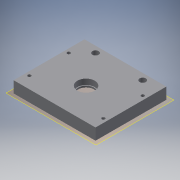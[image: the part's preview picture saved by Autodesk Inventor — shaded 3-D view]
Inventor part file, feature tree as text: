
AUTODESK INVENTOR PART (.ipt)
format: ipt  version: 2017 (Build 210142000, 142)  size: 169,472 bytes
history: native  units: mm
features: extrude x4, sketch x4, reference x2, projected_geometry x2, other x2, plane x1
ambient origin geometry x8: Origin, YZ Plane, XZ Plane, XY Plane, X Axis, Y Axis, Z Axis, Center Point
bodies: Solid1 (feature_tree)
feature tree (15):
  plane  "Work Plane1"
  extrude  "Extrusion1"  Depth=5.5mm TaperAngle=0.0deg
  extrude  "Extrusion2"  Depth=2.0mm TaperAngle=0.0deg
  extrude  "Extrusion3"  Depth=7.0mm TaperAngle=0.0deg
  extrude  "Extrusion4"  Depth=7.0mm
  sketch  "Sketch1"  dims[d0=76.0mm d1=5.5mm d2=0.0mm]
  reference  "Reference1"
  sketch  "Sketch2"  dims[d3=20.0mm d4=2.0mm d5=0.0mm]
  projected_geometry  "Projected Loop1"
  sketch  "Sketch3"  dims[d6=22.0mm d7=7.0mm d8=0.0mm]
  projected_geometry  "Projected Loop2"
  sketch  "Sketch4"  dims[d9=8.0mm d10=8.0mm d11=60.0mm d12=7.0mm d13=0.0mm]
  reference  "Reference2"
  other  "peristaltic pump.iam"
  other  "frame top:1"
